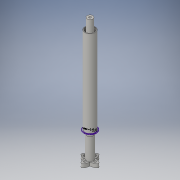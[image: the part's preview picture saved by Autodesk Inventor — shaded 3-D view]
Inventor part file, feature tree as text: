
AUTODESK INVENTOR PART (.ipt)
format: ipt  version: 2016 (Build 200138000, 138)  size: 155,648 bytes
history: native  units: in
note: dims shown in document units (in); Inventor stores cm internally (conversion verified against a paired STEP export)
features: sketch x10, extrude x5, fillet x2, hole x1, projected_geometry x1
ambient origin geometry x8: Origin, YZ Plane, XZ Plane, XY Plane, X Axis, Y Axis, Z Axis, Center Point
bodies: Solid1 (feature_tree)
feature tree (19):
  sketch  "Sketch1"  dims[d0=0.4646in d1=0.1693in]
  sketch  "Sketch2"  dims[d2=0.4646in d3=0.1693in]
  extrude  "Extrusion1"  Depth=0.4646in
  hole  "Hole1"  [1 undecoded]
  extrude  "Extrusion3"  Depth=0.1181in
  sketch  "Sketch6"  dims[d6=0.1181in d7=0.1181in d8=0.2756in]
  extrude  "Extrusion4"  Depth=0.1181in
  fillet  "Fillet1"  Radius=0.2756in
  sketch  "Sketch8"  dims[d14=0.1969in d15=0.0in]
  sketch  "Sketch9"  dims[d16=0.1181in d17=0.2362in d18=0.1575in d19=0.0787in d20=90.0deg d21=0.3937in d22=0.8108in d25=0.3937in]
  extrude  "Extrusion7"  Depth=0.2756in
  fillet  "Fillet4"  Radius=0.2756in
  sketch  "Sketch11"  dims[d26=0.2362in]
  sketch  "Sketch12"  dims[d27=1.1811in d28=0.0in]
  extrude  "Extrusion8"  Depth=0.3937in
  sketch  "Sketch5"  dims[d4=0.1181in d5=0.1181in]
  sketch  "Sketch7"  dims[d9=0.2756in d10=0.2756in d11=0.2756in]
  projected_geometry  "Projected Loop1"
  sketch  "Sketch13"  dims[d29=0.6299in d30=0.1969in d31=0.0in d32=0.2662in d33=0.6693in d34=0.563in d35=0.4843in d36=0.315in d44=0.1181in d45=4.7244in d46=0.0in d47=0.2037in d48=0.1181in d49=0.315in d50=0.5906in d51=0.0in]
note: 1 required parameter value undecoded (feature->parameter linkage not recoverable at this tier; creation-order binding heuristic only, values carry confidence <= 0.55)
